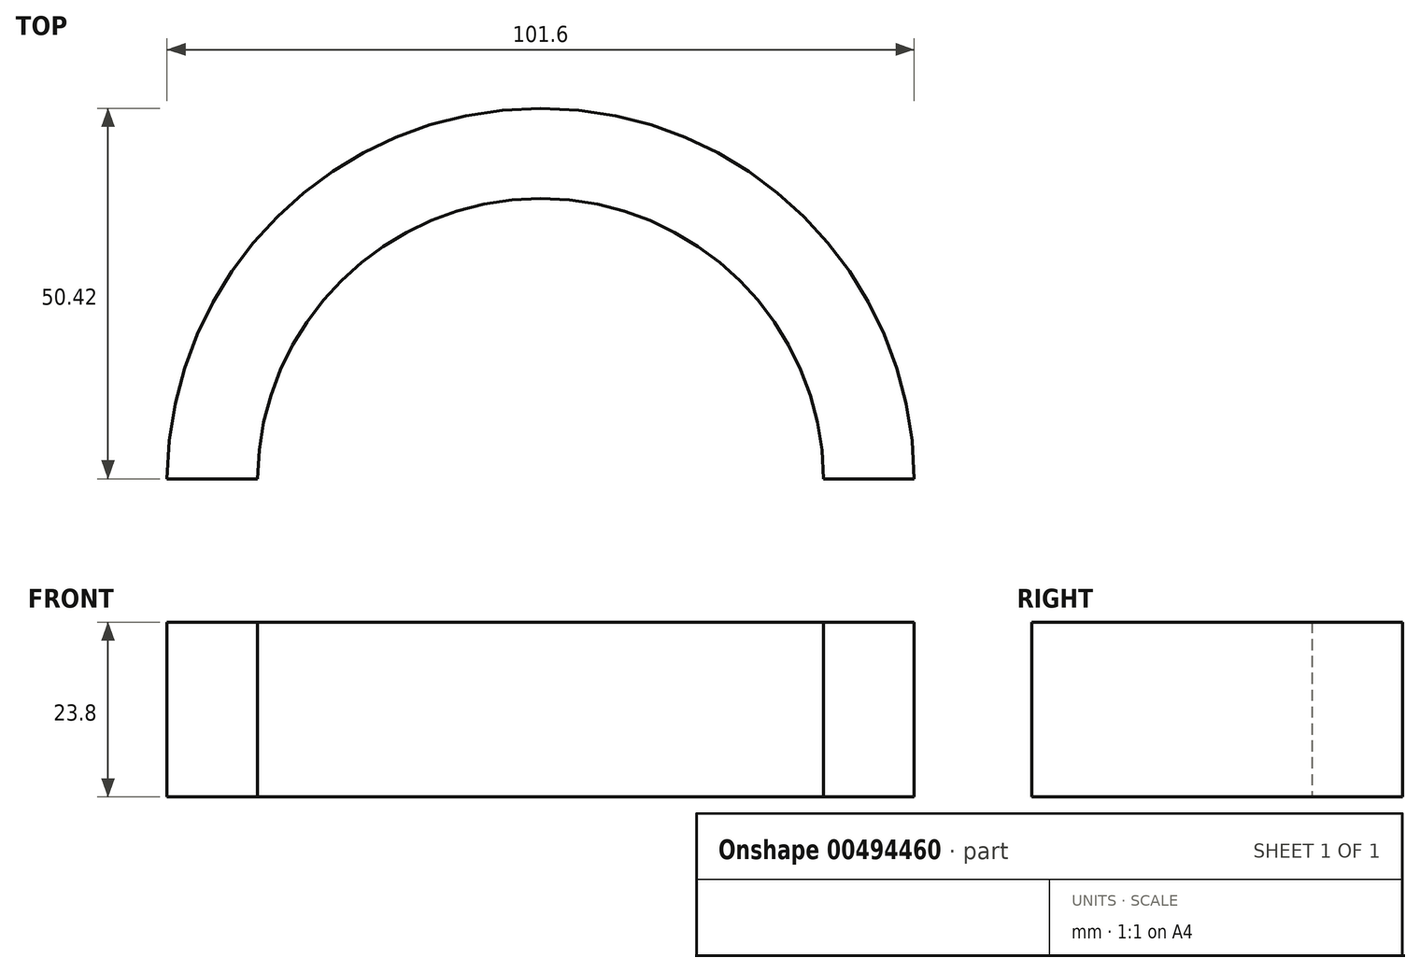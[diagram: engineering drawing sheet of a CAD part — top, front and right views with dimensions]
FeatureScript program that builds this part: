
annotation { "Feature Type Name" : "Feature", "Feature Type Description" : "" }
export const myFeature = defineFeature(function(context is Context, id is Id, definition is map)
    precondition{}
    {
        {
            var Q0;
            Q0=qCreatedBy(makeId("Top.planeOp"),FACE);
            var sketch = newSketch(context, id + "F0", { "sketchPlane" : qUnion([Q0])});
            skArc(sketch, "E0", {"start": v(38.5, 0.38) * mm, "mid": v(0, 38.5) * mm, "end": v(-38.5, 0.38) * mm});
            skArc(sketch, "E1", {"start": v(50.8, 0.38) * mm, "mid": v(0, 50.8) * mm, "end": v(-50.8, 0.38) * mm});
            skLineSegment(sketch, "E2.0", {"start": v(-50.8, 0.38) * mm, "end": v(-38.5, 0.38) * mm});
            skPoint(sketch, "E3.orphan", {"position": v(-50.8, 0) * mm});
            skLineSegment(sketch, "E4.trimOffspring", {"start": v(38.5, 0.38) * mm, "end": v(50.8, 0.38) * mm});
            skSolve(sketch);
        }
        {
            var Q0;
            {var subQ0=sQuery(id+"F0.wireOp",EDGE,"E0");Q0=makeQuery(id+"F0.imprint","IMPRINT",FACE,{"disambiguationData":[TD([[makeQuery(id+"F0.imprint","IMPRINT",EDGE,{"derivedFrom":subQ0}),-1.0]])]});}
            extrude(context, id + "F1", {"entities" : qUnion([Q0]), "depth" : 23.8 * mm});
        }
    });
